# Revit family: 2Registro regulador de vazao - DocolMatic
name_source: partatom
category: Conexões hidráulicas
revit_build: Autodesk Revit MEP 2014 (Build: 20131024_2115(x64)
units: mm (PartAtom-declared; Revit-internal decimal feet)

## types (2) — shared parameters
Diâmetro Nominal = 20  [stored 0.0656168 ft]
Docol: Ambiente = Hidráulicos
Docol: Bitola = 1/2"
Docol: Categoria = Registros
Docol: Fabricante = Docol
Docol: Linha = Registro Regulador de Vazão
Docol: Link do Produto = https://www.docol.com.br
Docol: Temperatura Máxima = 70 °C
Elevação-padrão = 2100
Fabricante = Docol
Raio Nominal = 10  [stored 0.0328084 ft]
URL = www.docol.com.br

## per-type parameters (varying)
| type | Descrição | Docol: Acabamento | Docol: Código | Docol: Descrição | Modelo |
| Metálico | Registro regulador de vazão metálico 1/2" - DocolMatic | Cromado | 13010006 | Registro regulador de vazão metálico 1/2" - DocolMatic | 13010006 |
| Standard | Registro regulador de vazão standard 1/2" - DocolMatic | Branco | 13030023 | Registro regulador de vazão standard 1/2" - DocolMatic | 13030023 |

note: [stored X ft] marks values corroborated as IEEE doubles in the binary element streams (Revit-internal decimal feet)

## geometry (parser evidence)
native form markers: Sweep x1
no freeform markers — native parametric forms only
